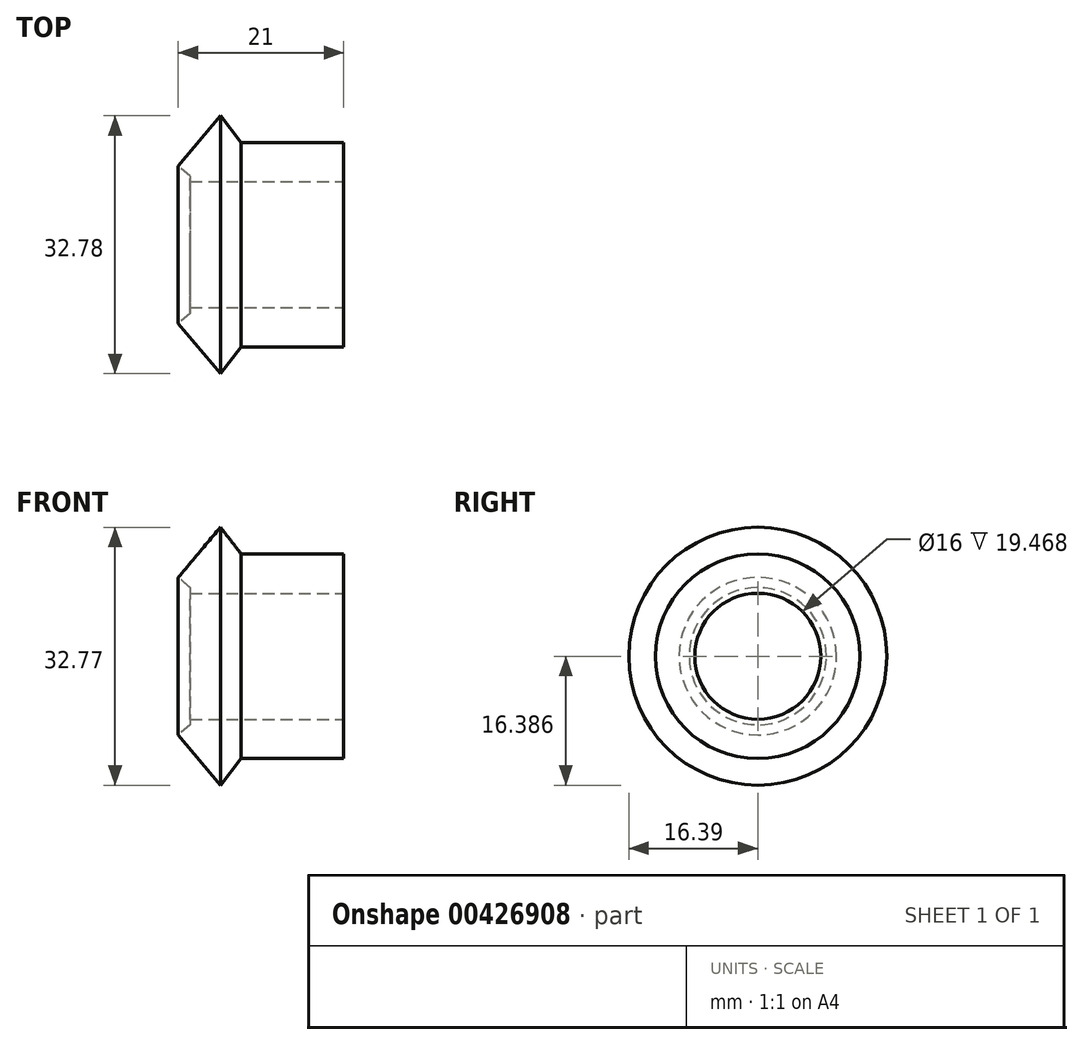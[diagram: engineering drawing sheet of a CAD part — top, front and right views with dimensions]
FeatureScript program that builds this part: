
annotation { "Feature Type Name" : "Feature", "Feature Type Description" : "" }
export const myFeature = defineFeature(function(context is Context, id is Id, definition is map)
    precondition{}
    {
        {
            var Q0;
            Q0=qCreatedBy(makeId("Front.planeOp"),FACE);
            var sketch = newSketch(context, id + "F0", { "sketchPlane" : qUnion([Q0])});
            skLineSegment(sketch, "E0", {"start": v(-60.22, 12.01) * mm, "end": v(-60.22, 25.01) * mm});
            skLineSegment(sketch, "E1", {"start": v(-60.22, 25.01) * mm, "end": v(-73.22, 25.01) * mm});
            skLineSegment(sketch, "E2", {"start": v(-147.66, -4.17) * mm, "end": v(-142.3, 2.21) * mm});
            skLineSegment(sketch, "E3", {"start": v(-146.12, -14.17) * mm, "end": v(-126.66, -14.17) * mm});
            skLineSegment(sketch, "E4", {"start": v(-126.66, -14.17) * mm, "end": v(-126.66, -1.17) * mm});
            skLineSegment(sketch, "E5", {"start": v(-126.66, -1.17) * mm, "end": v(-139.66, -1.17) * mm});
            skLineSegment(sketch, "E6", {"start": v(-142.3, 2.21) * mm, "end": v(-139.66, -1.17) * mm});
            skLineSegment(sketch, "E7", {"start": v(-147.66, -4.17) * mm, "end": v(-146.12, -5.46) * mm});
            skLineSegment(sketch, "E8", {"start": v(-146.12, -5.46) * mm, "end": v(-146.12, -14.17) * mm});
            skSolve(sketch);
        }
        {
            var Q0;
            Q0=makeQuery(id+"F0.imprint","IMPRINT",FACE,{"disambiguationData":[TD([[makeQuery(id+"F0.imprint","IMPRINT",EDGE,{"derivedFrom":sQuery(id+"F0.wireOp",EDGE,"E2")}),-1.0]])]});
            var Q1;
            Q1=sQuery(id+"F0.wireOp",EDGE,"E3");
            revolve(context, id + "F1", {"entities" : qUnion([Q0]), "axis" : qUnion([Q1]), "revolveType" : RevolveType.FULL});
        }
        {
            var Q0;
            Q0=makeQuery(id+"F1.opRevolve","SWEPT_FACE",FACE,{"disambiguationData":[OSD([sQuery(id+"F0.wireOp",EDGE,"E4")])]});
            var sketch = newSketch(context, id + "F2", { "sketchPlane" : qUnion([Q0])});
            skCircle(sketch, "E9", {"center": v(0, -14.17) * mm, "radius": 8 * mm});
            skSolve(sketch);
        }
        {
            var Q0;
            Q0=makeQuery(id+"F2.imprint","IMPRINT",FACE,{"disambiguationData":[TD([[makeQuery(id+"F2.imprint","IMPRINT",EDGE,{"derivedFrom":sQuery(id+"F2.wireOp",EDGE,"E9")}),1.0]])]});
            extrude(context, id + "F3", {"entities" : qUnion([Q0]), "operationType" : NewBodyOperationType.REMOVE, "endBound" : BoundingType.THROUGH_ALL, "oppositeDirection" : true, "depth" : 25 * mm});
        }
    });
